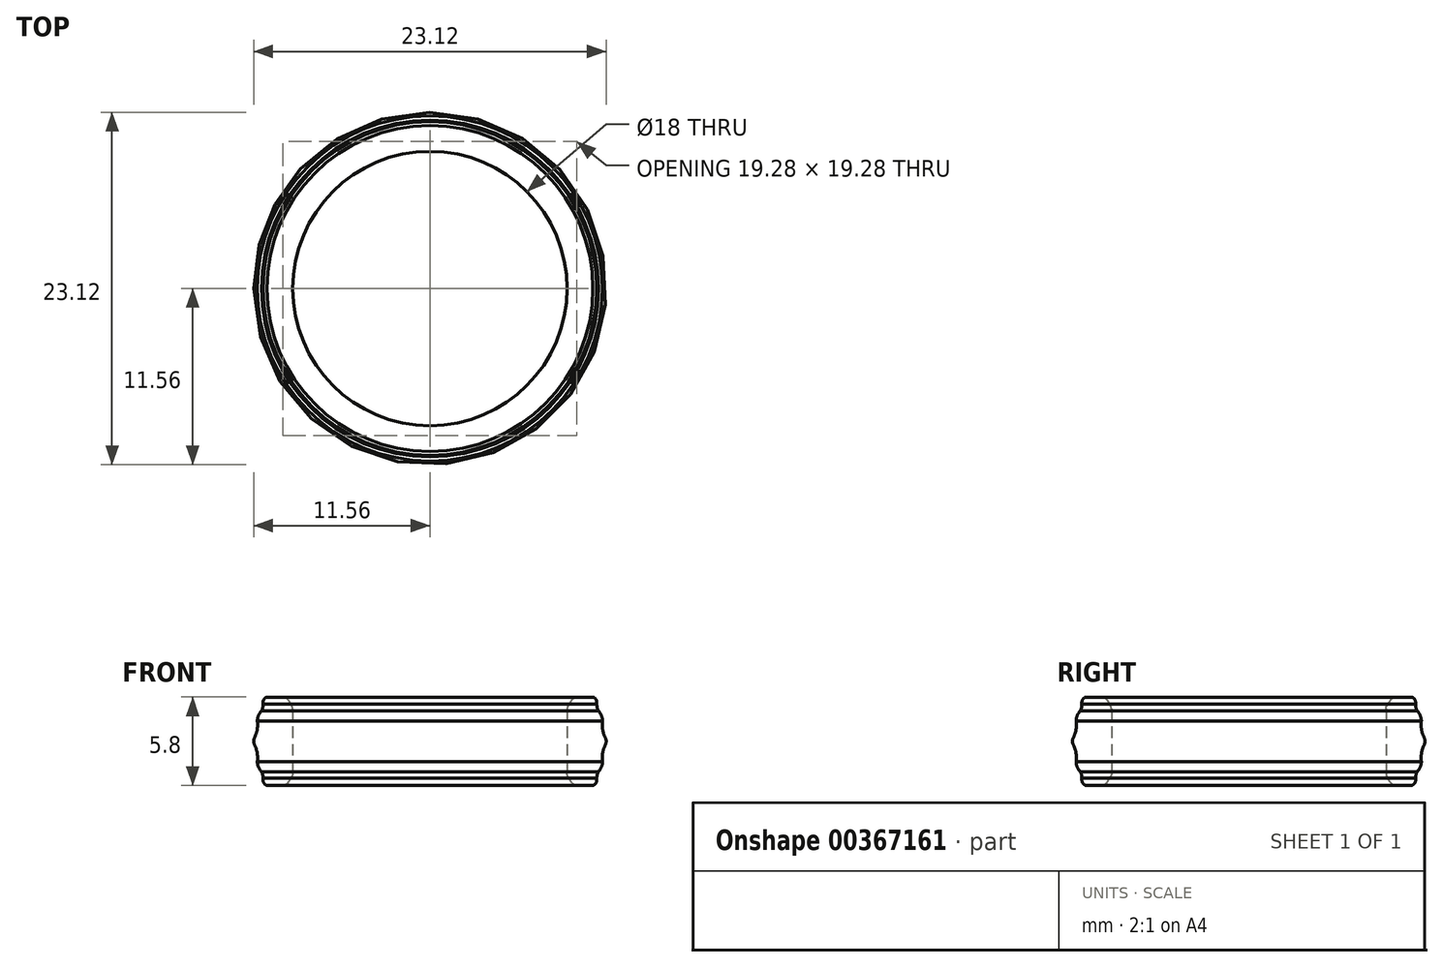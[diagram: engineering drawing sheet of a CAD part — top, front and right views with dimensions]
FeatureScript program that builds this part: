
annotation { "Feature Type Name" : "Feature", "Feature Type Description" : "" }
export const myFeature = defineFeature(function(context is Context, id is Id, definition is map)
    precondition{}
    {
        {
            var Q0;
            Q0=qCreatedBy(makeId("Front.planeOp"),FACE);
            var sketch = newSketch(context, id + "F0", { "sketchPlane" : qUnion([Q0])});
            skLineSegment(sketch, "E0.bottom", {"start": v(9, 0) * mm, "end": v(11, 0) * mm});
            skLineSegment(sketch, "E0.left", {"start": v(9, 0) * mm, "end": v(9, 2.21) * mm});
            skEllipticalArc(sketch, "E1", {});
            skArc(sketch, "E2", {"start": v(10.94, 2.57) * mm, "mid": v(10.87, 2.77) * mm, "end": v(10.7, 2.9) * mm});
            skArc(sketch, "E3", {"start": v(11.56, 0) * mm, "mid": v(11.54, 0.13) * mm, "end": v(11.5, 0.25) * mm});
            skLineSegment(sketch, "E4", {"start": v(11, 0) * mm, "end": v(11.56, 0) * mm});
            skLineSegment(sketch, "E5", {"start": v(0, 0) * mm, "end": v(0, 1.97) * mm, "construction": true});
            skLineSegment(sketch, "E6", {"start": v(10.7, 2.9) * mm, "end": v(9.45, 2.9) * mm});
            skArc(sketch, "E7", {"start": v(10.95, 2.43) * mm, "mid": v(10.97, 2.2) * mm, "end": v(11.05, 2) * mm});
            skLineSegment(sketch, "E8", {"start": v(10.94, 2.57) * mm, "end": v(10.95, 2.43) * mm});
            skArc(sketch, "E9", {"start": v(11.32, 1.33) * mm, "mid": v(11.33, 0.78) * mm, "end": v(11.5, 0.25) * mm});
            skPoint(sketch, "E10.center.orphan", {"position": v(10, 0) * mm});
            skArc(sketch, "E11", {"start": v(11.32, 1.33) * mm, "mid": v(11.24, 1.7) * mm, "end": v(11.05, 2) * mm});
            const initialGuessF0  = {"E1": [0.00945449541933838, 0.0020175722270351004, -0.4573021954639456, -0.889311363934958, 0.001375739801042828, 0.0004944153759990667, 4.110990621748758, 4.736122492673656]};
            skSetInitialGuess(sketch, initialGuessF0);
            skSolve(sketch);
        }
        {
            var Q0;
            Q0=makeQuery(id+"F0.imprint","IMPRINT",FACE,{"disambiguationData":[TD([[makeQuery(id+"F0.imprint","IMPRINT",EDGE,{"derivedFrom":sQuery(id+"F0.wireOp",EDGE,"E0.bottom")}),1.0]])]});
            var Q1;
            Q1=sQuery(id+"F0.wireOp",EDGE,"E5");
            revolve(context, id + "F1", {"entities" : qUnion([Q0]), "axis" : qUnion([Q1]), "revolveType" : RevolveType.FULL});
        }
        {
            var Q0;
            Q0=makeQuery(id+"F1.opRevolve","SWEPT_EDGE",EDGE,{"disambiguationData":[OSD([sQuery(id+"F0.wireOp",EDGE,"E0.left"),sQuery(id+"F0.wireOp",EDGE,"E1")])]});
            var Q1;
            Q1=makeQuery(id+"F1.opRevolve","SWEPT_EDGE",EDGE,{"disambiguationData":[OSD([sQuery(id+"F0.wireOp",EDGE,"E0.top"),sQuery(id+"F0.wireOp",EDGE,"E1")])]});
            var Q2;
            Q2=makeQuery(id+"F1.opRevolve","SWEPT_EDGE",EDGE,{"disambiguationData":[OSD([sQuery(id+"F0.wireOp",EDGE,"E0.top"),sQuery(id+"F0.wireOp",EDGE,"abeecfbf-6f53-427e-97c1-011e85bba14e.trimOffspring")])]});
            fillet(context, id + "F2", {"entities" : qUnion([Q0, Q1, Q2]), "radius" : 0.4 * mm, "tangentPropagation" : true, "allowEdgeOverflow" : false});
        }
        {
            var Q0;
            Q0=makeQuery(id+"F1.opRevolve","SWEPT_BODY",BODY,{"disambiguationData":[OSD([sQuery(id+"F0.wireOp",EDGE,"E0.bottom"),sQuery(id+"F0.wireOp",EDGE,"E0.left"),sQuery(id+"F0.wireOp",EDGE,"E1"),sQuery(id+"F0.wireOp",EDGE,"E2"),sQuery(id+"F0.wireOp",EDGE,"E3"),sQuery(id+"F0.wireOp",EDGE,"E4"),sQuery(id+"F0.wireOp",EDGE,"E6"),sQuery(id+"F0.wireOp",EDGE,"E7"),sQuery(id+"F0.wireOp",EDGE,"E8"),sQuery(id+"F0.wireOp",EDGE,"E9"),sQuery(id+"F0.wireOp",EDGE,"E11")])]});
            var Q1;
            Q1=qCreatedBy(makeId("Top.planeOp"),FACE);
            mirror(context, id + "F3", {"operationType" : NewBodyOperationType.ADD, "entities" : qUnion([Q0]), "mirrorPlane" : qUnion([Q1])});
        }
    });
